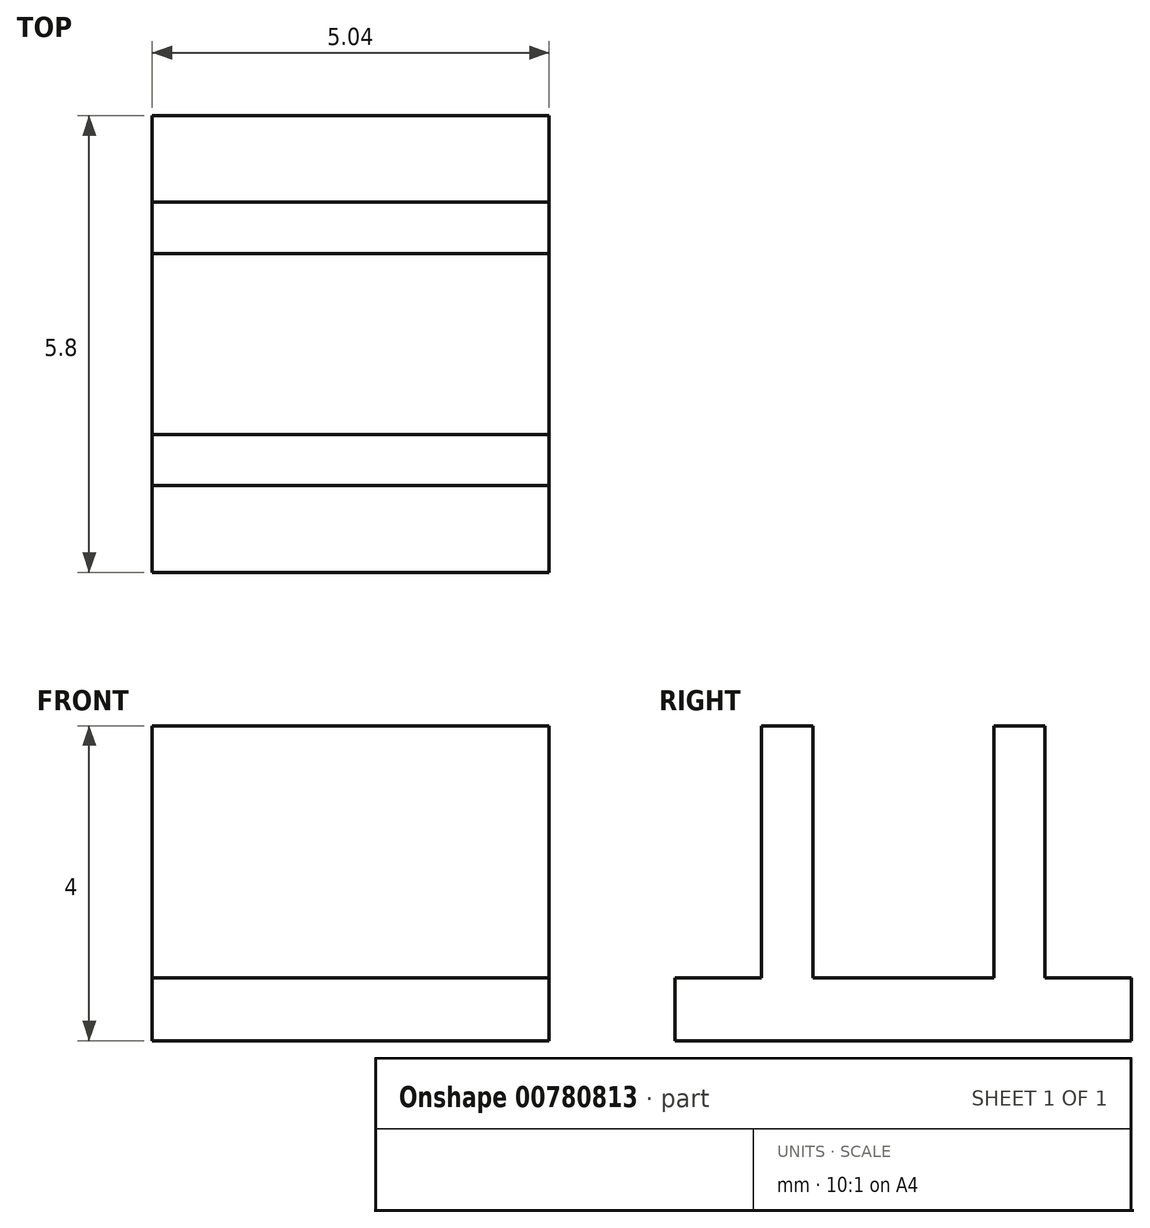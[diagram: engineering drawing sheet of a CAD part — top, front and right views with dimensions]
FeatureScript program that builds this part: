
annotation { "Feature Type Name" : "Feature", "Feature Type Description" : "" }
export const myFeature = defineFeature(function(context is Context, id is Id, definition is map)
    precondition{}
    {
        {
            var Q0;
            Q0=qCreatedBy(makeId("Top.planeOp"),FACE);
            var sketch = newSketch(context, id + "F0", { "sketchPlane" : qUnion([Q0])});
            skLineSegment(sketch, "E0.bottom", {"start": v(0, 0) * mm, "end": v(5.04, 0) * mm});
            skLineSegment(sketch, "E0.top", {"start": v(0, 5.8) * mm, "end": v(5.04, 5.8) * mm});
            skLineSegment(sketch, "E0.left", {"start": v(0, 0) * mm, "end": v(0, 5.8) * mm});
            skLineSegment(sketch, "E0.right", {"start": v(5.04, 0) * mm, "end": v(5.04, 5.8) * mm});
            skSolve(sketch);
        }
        {
            var Q0;
            Q0 = qSketchRegion(id + "F0", true);
            extrude(context, id + "F1", {"entities" : qUnion([Q0]), "depth" : .8 * mm, "offsetDistance" : 25 * mm});
        }
        {
            var Q0;
            Q0=makeQuery(id+"F1.opExtrude","CAP_FACE",FACE,{"disambiguationData":[OSD([sQuery(id+"F0.wireOp",EDGE,"E0.bottom"),sQuery(id+"F0.wireOp",EDGE,"E0.top"),sQuery(id+"F0.wireOp",EDGE,"E0.left"),sQuery(id+"F0.wireOp",EDGE,"E0.right")])],"isStart":false});
            var sketch = newSketch(context, id + "F2", { "sketchPlane" : qUnion([Q0])});
            skLineSegment(sketch, "E1.bottom", {"start": v(0, 4.7) * mm, "end": v(5.04, 4.7) * mm});
            skLineSegment(sketch, "E1.top", {"start": v(0, 4.05) * mm, "end": v(5.04, 4.05) * mm});
            skLineSegment(sketch, "E1.left", {"start": v(0, 4.7) * mm, "end": v(0, 4.05) * mm});
            skLineSegment(sketch, "E1.right", {"start": v(5.04, 4.7) * mm, "end": v(5.04, 4.05) * mm});
            skLineSegment(sketch, "E2.bottom", {"start": v(0, 1.75) * mm, "end": v(5.04, 1.75) * mm});
            skLineSegment(sketch, "E2.top", {"start": v(0, 1.1) * mm, "end": v(5.04, 1.1) * mm});
            skLineSegment(sketch, "E2.left", {"start": v(0, 1.75) * mm, "end": v(0, 1.1) * mm});
            skLineSegment(sketch, "E2.right", {"start": v(5.04, 1.75) * mm, "end": v(5.04, 1.1) * mm});
            skSolve(sketch);
        }
        {
            var Q0;
            Q0 = qSketchRegion(id + "F2", true);
            extrude(context, id + "F3", {"entities" : qUnion([Q0]), "operationType" : NewBodyOperationType.ADD, "depth" : 3.2 * mm, "offsetDistance" : 25 * mm});
        }
    });
